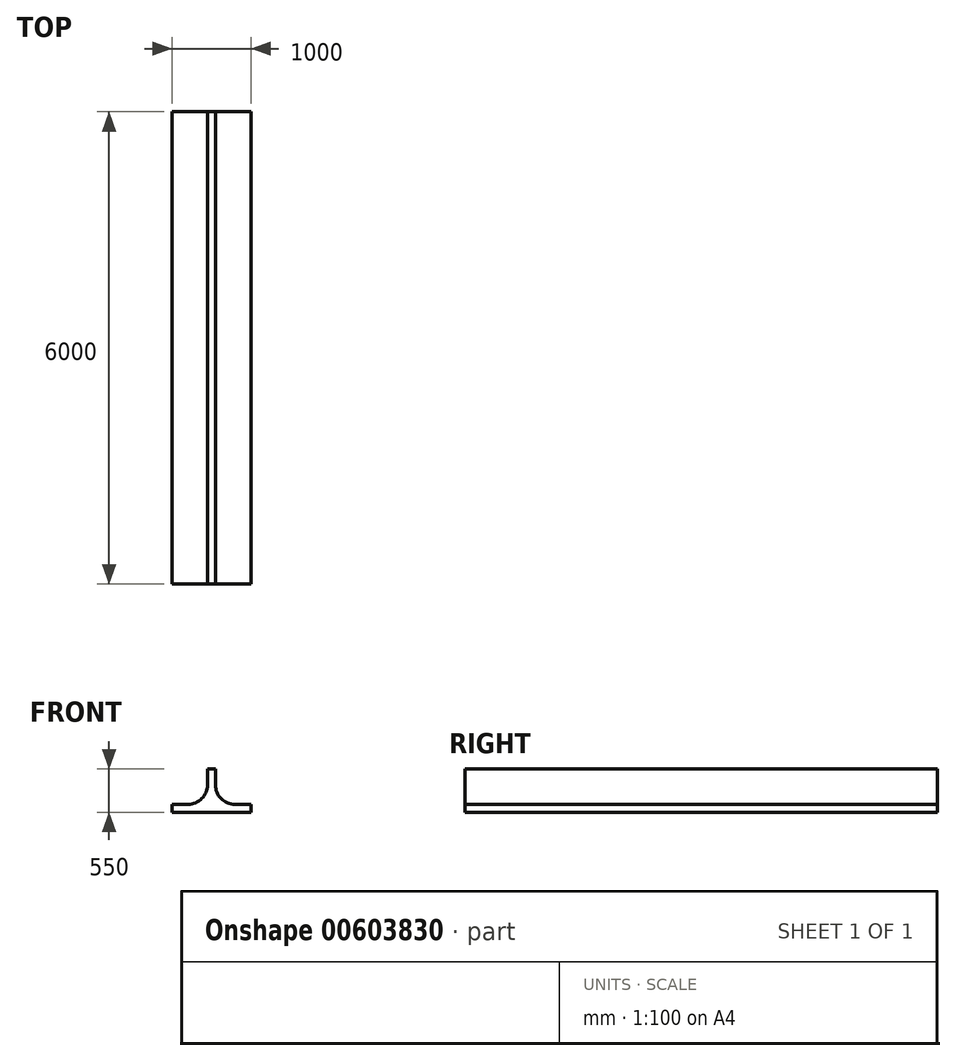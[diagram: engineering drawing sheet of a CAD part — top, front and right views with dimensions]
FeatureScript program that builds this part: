
annotation { "Feature Type Name" : "Feature", "Feature Type Description" : "" }
export const myFeature = defineFeature(function(context is Context, id is Id, definition is map)
    precondition{}
    {
        {
            var Q0;
            Q0=qCreatedBy(makeId("Front.planeOp"),FACE);
            var sketch = newSketch(context, id + "F0", { "sketchPlane" : qUnion([Q0])});
            skLineSegment(sketch, "E0", {"start": v(-50, 550) * mm, "end": v(-50, 100) * mm});
            skLineSegment(sketch, "E1", {"start": v(-50, 100) * mm, "end": v(-500, 100) * mm});
            skLineSegment(sketch, "E2", {"start": v(-500, 100) * mm, "end": v(-500, 0) * mm});
            skLineSegment(sketch, "E3", {"start": v(-500, 0) * mm, "end": v(500, 0) * mm});
            skLineSegment(sketch, "E4", {"start": v(500, 0) * mm, "end": v(500, 100) * mm});
            skLineSegment(sketch, "E5", {"start": v(500, 100) * mm, "end": v(50, 100) * mm});
            skLineSegment(sketch, "E6", {"start": v(50, 100) * mm, "end": v(50, 550) * mm});
            skLineSegment(sketch, "E7", {"start": v(50, 550) * mm, "end": v(-50, 550) * mm});
            skSolve(sketch);
        }
        {
            var Q0;
            Q0 = qSketchRegion(id + "F0", true);
            extrude(context, id + "F1", {"entities" : qUnion([Q0]), "depth" : 6000 * mm, "offsetDistance" : 25 * mm});
        }
        {
            var Q0;
            Q0=makeQuery(id+"F1.opExtrude","SWEPT_EDGE",EDGE,{"disambiguationData":[OSD([sQuery(id+"F0.wireOp",EDGE,"E0"),sQuery(id+"F0.wireOp",EDGE,"E1")])]});
            var Q1;
            Q1=makeQuery(id+"F1.opExtrude","SWEPT_EDGE",EDGE,{"disambiguationData":[OSD([sQuery(id+"F0.wireOp",EDGE,"E5"),sQuery(id+"F0.wireOp",EDGE,"E6")])]});
            fillet(context, id + "F2", {"entities" : qUnion([Q0, Q1]), "radius" : 250 * mm, "tangentPropagation" : true, "allowEdgeOverflow" : false});
        }
    });
